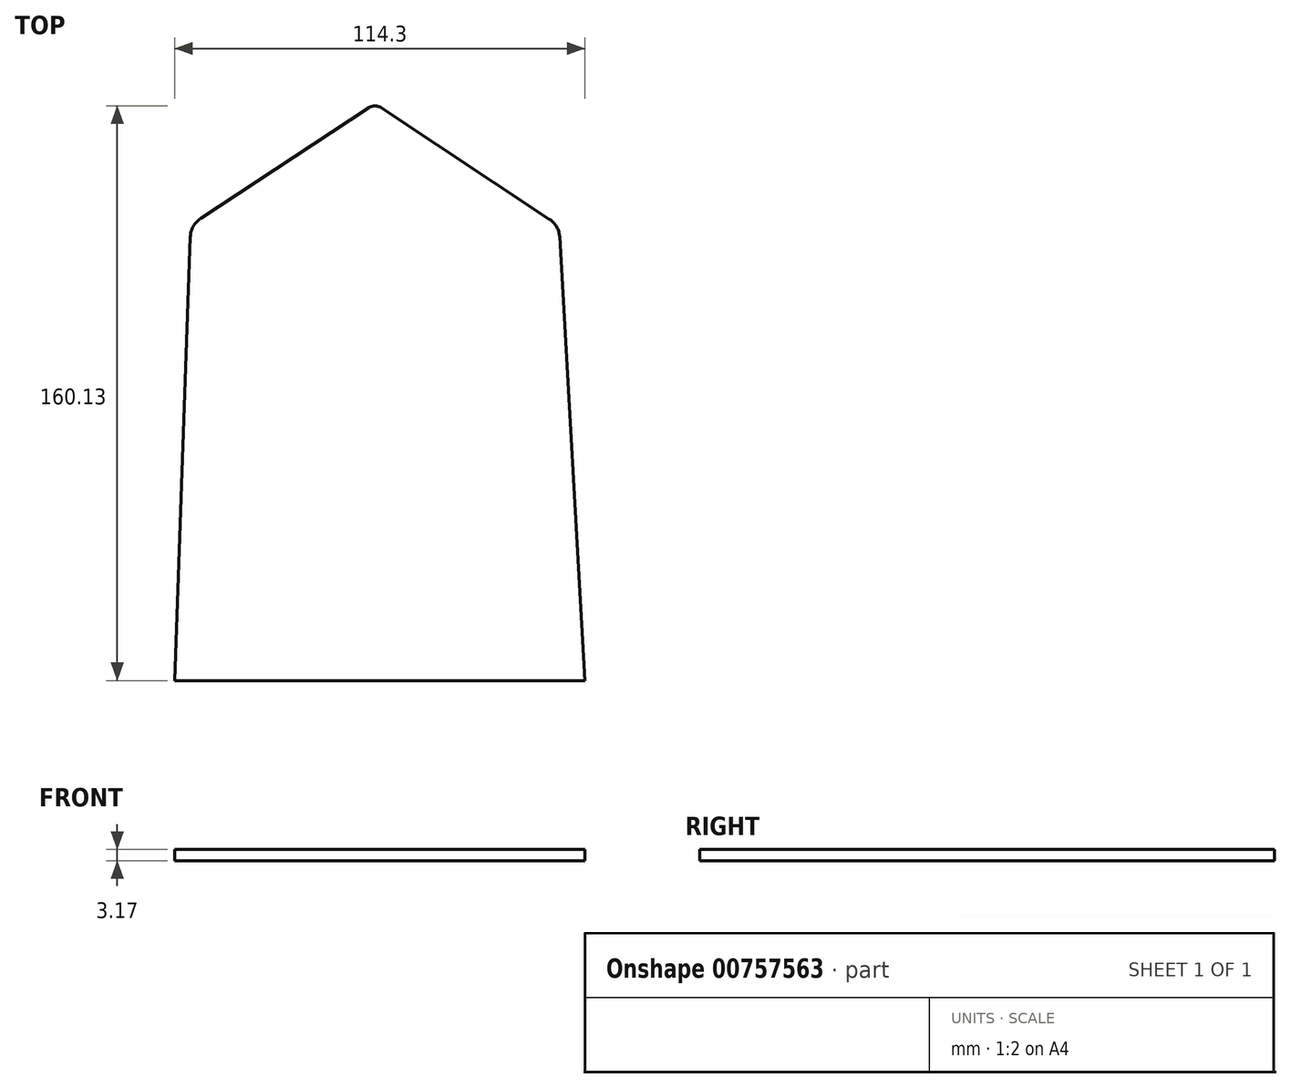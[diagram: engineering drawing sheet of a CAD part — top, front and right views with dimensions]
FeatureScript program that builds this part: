
annotation { "Feature Type Name" : "Feature", "Feature Type Description" : "" }
export const myFeature = defineFeature(function(context is Context, id is Id, definition is map)
    precondition{}
    {
        {
            var Q0;
            Q0=qCreatedBy(makeId("Top.planeOp"),FACE);
            var sketch = newSketch(context, id + "F0", { "sketchPlane" : qUnion([Q0])});
            skLineSegment(sketch, "E0", {"start": v(7.57, 121.66) * mm, "end": v(-39.3, 90.79) * mm});
            skLineSegment(sketch, "E1", {"start": v(57.94, 90.62) * mm, "end": v(11.07, 121.66) * mm});
            skPoint(sketch, "E2.visualSharp", {"position": v(-42.03, 88.99) * mm});
            skPoint(sketch, "E3.visualSharp", {"position": v(60.6, 88.86) * mm});
            skPoint(sketch, "E4.visualSharp", {"position": v(9.32, 122.82) * mm});
            skArc(sketch, "E4.filletArc", {"start": v(11.07, 121.66) * mm, "mid": v(9.32, 122.19) * mm, "end": v(7.57, 121.66) * mm});
            skLineSegment(sketch, "E5", {"start": v(-42.15, 85.7) * mm, "end": v(-46.5, -37.94) * mm});
            skLineSegment(sketch, "E6", {"start": v(-46.5, -37.94) * mm, "end": v(10.65, -37.94) * mm});
            skLineSegment(sketch, "E7", {"start": v(10.65, -37.94) * mm, "end": v(67.8, -37.94) * mm});
            skLineSegment(sketch, "E8", {"start": v(67.8, -37.94) * mm, "end": v(60.77, 85.68) * mm});
            skLineSegment(sketch, "E9", {"start": v(9.32, 122.82) * mm, "end": v(10.65, -37.94) * mm, "construction": true});
            skArc(sketch, "E10.filletArc", {"start": v(-39.3, 90.79) * mm, "mid": v(-41.34, 88.6) * mm, "end": v(-42.15, 85.7) * mm});
            skArc(sketch, "E11.filletArc", {"start": v(60.77, 85.68) * mm, "mid": v(59.94, 88.48) * mm, "end": v(57.94, 90.62) * mm});
            skSolve(sketch);
        }
        {
            var Q0;
            Q0=qSketchRegion(id+"F0",true);
            extrude(context, id + "F1", {"entities" : qUnion([Q0]), "depth" : 3.17 * mm, "offsetDistance" : 25.4 * mm});
        }
    });
